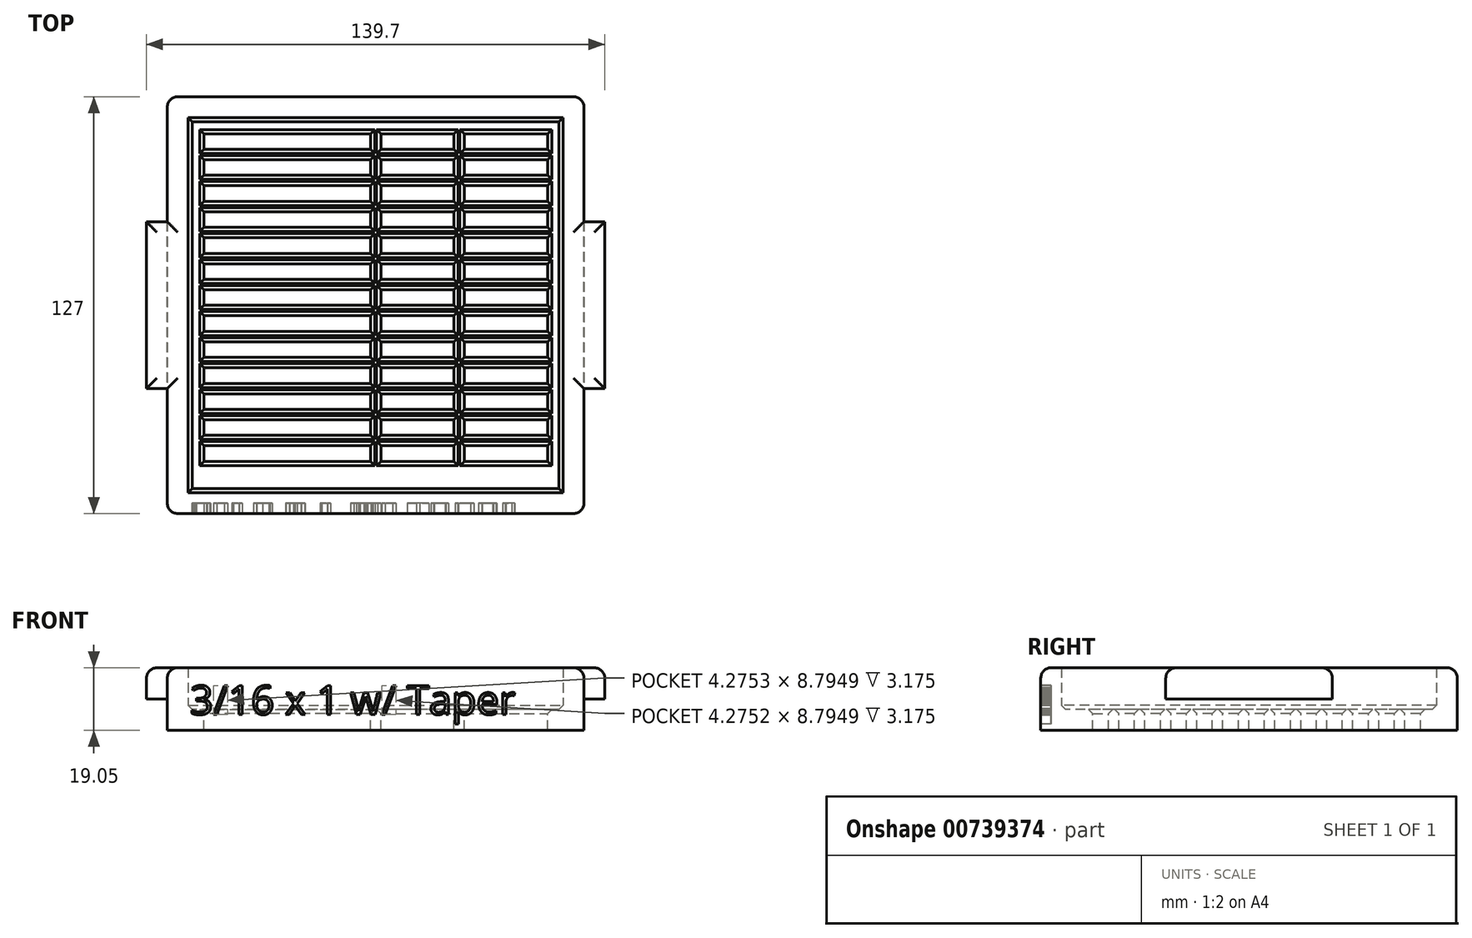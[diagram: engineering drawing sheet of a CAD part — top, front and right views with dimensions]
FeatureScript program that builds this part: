
annotation { "Feature Type Name" : "Feature", "Feature Type Description" : "" }
export const myFeature = defineFeature(function(context is Context, id is Id, definition is map)
    precondition{}
    {
        {
            var Q0;
            Q0=qCreatedBy(makeId("Top.planeOp"),FACE);
            var sketch = newSketch(context, id + "F0", { "sketchPlane" : qUnion([Q0])});
            skLineSegment(sketch, "E0.bottom", {"start": v(-63.5, -63.76) * mm, "end": v(63.5, -63.76) * mm});
            skLineSegment(sketch, "E0.top", {"start": v(-63.5, 63.24) * mm, "end": v(63.5, 63.24) * mm});
            skLineSegment(sketch, "E0.left", {"start": v(-63.5, -63.76) * mm, "end": v(-63.5, 63.24) * mm});
            skLineSegment(sketch, "E0.right", {"start": v(63.5, -63.76) * mm, "end": v(63.5, 63.24) * mm});
            skLineSegment(sketch, "E1.bottom", {"start": v(-57.15, -57.4) * mm, "end": v(57.15, -57.4) * mm});
            skLineSegment(sketch, "E1.top", {"start": v(-57.15, 56.9) * mm, "end": v(57.15, 56.9) * mm});
            skLineSegment(sketch, "E1.left", {"start": v(-57.15, -57.4) * mm, "end": v(-57.15, 56.9) * mm});
            skLineSegment(sketch, "E1.right", {"start": v(57.15, -57.4) * mm, "end": v(57.15, 56.9) * mm});
            skPoint(sketch, "E2", {"position": v(-63.5, -0.26) * mm});
            skPoint(sketch, "E3", {"position": v(63.5, -0.26) * mm});
            skLineSegment(sketch, "E4.bottom", {"start": v(-69.85, 25.14) * mm, "end": v(-57.15, 25.14) * mm});
            skLineSegment(sketch, "E4.top", {"start": v(-69.85, -25.66) * mm, "end": v(-57.15, -25.66) * mm});
            skLineSegment(sketch, "E4.left", {"start": v(-69.85, 25.14) * mm, "end": v(-69.85, -25.66) * mm});
            skLineSegment(sketch, "E4.right", {"start": v(-57.15, 25.14) * mm, "end": v(-57.15, -25.66) * mm});
            skLineSegment(sketch, "E5.bottom", {"start": v(69.85, 25.14) * mm, "end": v(57.15, 25.14) * mm});
            skLineSegment(sketch, "E5.top", {"start": v(69.85, -25.66) * mm, "end": v(57.15, -25.66) * mm});
            skLineSegment(sketch, "E5.left", {"start": v(69.85, 25.14) * mm, "end": v(69.85, -25.66) * mm});
            skLineSegment(sketch, "E5.right", {"start": v(57.15, 25.14) * mm, "end": v(57.15, -25.66) * mm});
            skPoint(sketch, "E5.cornerSnap0", {"position": v(-63.5, 25.14) * mm});
            skSolve(sketch);
        }
        {
            var Q0;
            {var subQ3=sQuery(id+"F0.wireOp",EDGE,"E1.bottom");Q0=makeQuery(id+"F0.imprint","IMPRINT",FACE,{"disambiguationData":[TD([[makeQuery(id+"F0.imprint","IMPRINT",EDGE,{"derivedFrom":subQ3}),1.0]])]});}
            extrude(context, id + "F1", {"entities" : qUnion([Q0]), "depth" : 6.35 * mm, "offsetDistance" : 25.4 * mm});
        }
        {
            var Q0;
            Q0=qSketchRegion(id+"F0",true);
            extrude(context, id + "F2", {"entities" : qUnion([Q0]), "operationType" : NewBodyOperationType.ADD, "depth" : 19.05 * mm, "offsetDistance" : 25.4 * mm});
        }
        {
            var Q0;
            Q0=makeQuery(id+"F1.opExtrude","CAP_FACE",FACE,{"disambiguationData":[OSD([sQuery(id+"F0.wireOp",EDGE,"E1.bottom"),sQuery(id+"F0.wireOp",EDGE,"E1.top"),sQuery(id+"F0.wireOp",EDGE,"E1.left"),sQuery(id+"F0.wireOp",EDGE,"E1.right"),sQuery(id+"F0.wireOp",EDGE,"E4.right"),sQuery(id+"F0.wireOp",EDGE,"E5.right")])],"isStart":false});
            var sketch = newSketch(context, id + "F3", { "sketchPlane" : qUnion([Q0])});
            skLineSegment(sketch, "E6.bottom", {"start": v(-52.4, -47.88) * mm, "end": v(-23.83, -47.88) * mm});
            skLineSegment(sketch, "E6.top", {"start": v(-52.4, -43.13) * mm, "end": v(-23.83, -43.13) * mm});
            skLineSegment(sketch, "E6.left", {"start": v(-52.4, -47.88) * mm, "end": v(-52.4, -43.13) * mm});
            skLineSegment(sketch, "E6.right", {"start": v(-23.83, -47.88) * mm, "end": v(-23.83, -43.13) * mm});
            skLineSegment(sketch, "E7.0.1.0", {"start": v(-52.4, -39.96) * mm, "end": v(-23.83, -39.96) * mm});
            skLineSegment(sketch, "E7.0.1.1", {"start": v(-52.4, -35.2) * mm, "end": v(-23.83, -35.2) * mm});
            skLineSegment(sketch, "E7.0.1.2", {"start": v(-52.4, -39.96) * mm, "end": v(-52.4, -35.2) * mm});
            skLineSegment(sketch, "E7.0.1.3", {"start": v(-23.83, -39.96) * mm, "end": v(-23.83, -35.2) * mm});
            skLineSegment(sketch, "E7.0.2.0", {"start": v(-52.4, -32.03) * mm, "end": v(-23.83, -32.03) * mm});
            skLineSegment(sketch, "E7.0.2.1", {"start": v(-52.4, -27.28) * mm, "end": v(-23.83, -27.28) * mm});
            skLineSegment(sketch, "E7.0.2.2", {"start": v(-52.4, -32.03) * mm, "end": v(-52.4, -27.28) * mm});
            skLineSegment(sketch, "E7.0.2.3", {"start": v(-23.83, -32.03) * mm, "end": v(-23.83, -27.28) * mm});
            skLineSegment(sketch, "E7.0.3.0", {"start": v(-52.4, -24.1) * mm, "end": v(-23.83, -24.1) * mm});
            skLineSegment(sketch, "E7.0.3.1", {"start": v(-52.4, -19.36) * mm, "end": v(-23.83, -19.36) * mm});
            skLineSegment(sketch, "E7.0.3.2", {"start": v(-52.4, -24.1) * mm, "end": v(-52.4, -19.36) * mm});
            skLineSegment(sketch, "E7.0.3.3", {"start": v(-23.83, -24.1) * mm, "end": v(-23.83, -19.36) * mm});
            skLineSegment(sketch, "E7.0.4.0", {"start": v(-52.4, -16.18) * mm, "end": v(-23.83, -16.18) * mm});
            skLineSegment(sketch, "E7.0.4.1", {"start": v(-52.4, -11.43) * mm, "end": v(-23.83, -11.43) * mm});
            skLineSegment(sketch, "E7.0.4.2", {"start": v(-52.4, -16.18) * mm, "end": v(-52.4, -11.43) * mm});
            skLineSegment(sketch, "E7.0.4.3", {"start": v(-23.83, -16.18) * mm, "end": v(-23.83, -11.43) * mm});
            skLineSegment(sketch, "E7.0.5.0", {"start": v(-52.4, -8.26) * mm, "end": v(-23.83, -8.26) * mm});
            skLineSegment(sketch, "E7.0.5.1", {"start": v(-52.4, -3.5) * mm, "end": v(-23.83, -3.5) * mm});
            skLineSegment(sketch, "E7.0.5.2", {"start": v(-52.4, -8.26) * mm, "end": v(-52.4, -3.5) * mm});
            skLineSegment(sketch, "E7.0.5.3", {"start": v(-23.83, -8.26) * mm, "end": v(-23.83, -3.5) * mm});
            skLineSegment(sketch, "E7.0.6.0", {"start": v(-52.4, -0.33) * mm, "end": v(-23.83, -0.33) * mm});
            skLineSegment(sketch, "E7.0.6.1", {"start": v(-52.4, 4.42) * mm, "end": v(-23.83, 4.42) * mm});
            skLineSegment(sketch, "E7.0.6.2", {"start": v(-52.4, -0.33) * mm, "end": v(-52.4, 4.42) * mm});
            skLineSegment(sketch, "E7.0.6.3", {"start": v(-23.83, -0.33) * mm, "end": v(-23.83, 4.42) * mm});
            skLineSegment(sketch, "E7.0.7.0", {"start": v(-52.4, 7.6) * mm, "end": v(-23.83, 7.6) * mm});
            skLineSegment(sketch, "E7.0.7.1", {"start": v(-52.4, 12.34) * mm, "end": v(-23.83, 12.34) * mm});
            skLineSegment(sketch, "E7.0.7.2", {"start": v(-52.4, 7.6) * mm, "end": v(-52.4, 12.34) * mm});
            skLineSegment(sketch, "E7.0.7.3", {"start": v(-23.83, 7.6) * mm, "end": v(-23.83, 12.34) * mm});
            skLineSegment(sketch, "E7.0.8.0", {"start": v(-52.4, 15.51) * mm, "end": v(-23.83, 15.51) * mm});
            skLineSegment(sketch, "E7.0.8.1", {"start": v(-52.4, 20.26) * mm, "end": v(-23.83, 20.26) * mm});
            skLineSegment(sketch, "E7.0.8.2", {"start": v(-52.4, 15.51) * mm, "end": v(-52.4, 20.26) * mm});
            skLineSegment(sketch, "E7.0.8.3", {"start": v(-23.83, 15.51) * mm, "end": v(-23.83, 20.26) * mm});
            skLineSegment(sketch, "E7.0.9.0", {"start": v(-52.4, 23.44) * mm, "end": v(-23.83, 23.44) * mm});
            skLineSegment(sketch, "E7.0.9.1", {"start": v(-52.4, 28.19) * mm, "end": v(-23.83, 28.19) * mm});
            skLineSegment(sketch, "E7.0.9.2", {"start": v(-52.4, 23.44) * mm, "end": v(-52.4, 28.19) * mm});
            skLineSegment(sketch, "E7.0.9.3", {"start": v(-23.83, 23.44) * mm, "end": v(-23.83, 28.19) * mm});
            skLineSegment(sketch, "E7.0.10.0", {"start": v(-52.4, 31.36) * mm, "end": v(-23.83, 31.36) * mm});
            skLineSegment(sketch, "E7.0.10.1", {"start": v(-52.4, 36.11) * mm, "end": v(-23.83, 36.11) * mm});
            skLineSegment(sketch, "E7.0.10.2", {"start": v(-52.4, 31.36) * mm, "end": v(-52.4, 36.11) * mm});
            skLineSegment(sketch, "E7.0.10.3", {"start": v(-23.83, 31.36) * mm, "end": v(-23.83, 36.11) * mm});
            skLineSegment(sketch, "E7.0.11.0", {"start": v(-52.4, 39.29) * mm, "end": v(-23.83, 39.29) * mm});
            skLineSegment(sketch, "E7.0.11.1", {"start": v(-52.4, 44.04) * mm, "end": v(-23.83, 44.04) * mm});
            skLineSegment(sketch, "E7.0.11.2", {"start": v(-52.4, 39.29) * mm, "end": v(-52.4, 44.04) * mm});
            skLineSegment(sketch, "E7.0.11.3", {"start": v(-23.83, 39.29) * mm, "end": v(-23.83, 44.04) * mm});
            skLineSegment(sketch, "E7.0.12.0", {"start": v(-52.4, 47.21) * mm, "end": v(-23.83, 47.21) * mm});
            skLineSegment(sketch, "E7.0.12.1", {"start": v(-52.4, 51.96) * mm, "end": v(-23.83, 51.96) * mm});
            skLineSegment(sketch, "E7.0.12.2", {"start": v(-52.4, 47.21) * mm, "end": v(-52.4, 51.96) * mm});
            skLineSegment(sketch, "E7.0.12.3", {"start": v(-23.83, 47.21) * mm, "end": v(-23.83, 51.96) * mm});
            skLineSegment(sketch, "E7.1.0.0", {"start": v(-27, -47.88) * mm, "end": v(1.57, -47.88) * mm});
            skLineSegment(sketch, "E7.1.0.1", {"start": v(-27, -43.13) * mm, "end": v(1.57, -43.13) * mm});
            skLineSegment(sketch, "E7.1.0.2", {"start": v(-27, -47.88) * mm, "end": v(-27, -43.13) * mm});
            skLineSegment(sketch, "E7.1.0.3", {"start": v(1.57, -47.88) * mm, "end": v(1.57, -43.13) * mm});
            skLineSegment(sketch, "E7.1.1.0", {"start": v(-27, -39.96) * mm, "end": v(1.57, -39.96) * mm});
            skLineSegment(sketch, "E7.1.1.1", {"start": v(-27, -35.2) * mm, "end": v(1.57, -35.2) * mm});
            skLineSegment(sketch, "E7.1.1.2", {"start": v(-27, -39.96) * mm, "end": v(-27, -35.2) * mm});
            skLineSegment(sketch, "E7.1.1.3", {"start": v(1.57, -39.96) * mm, "end": v(1.57, -35.2) * mm});
            skLineSegment(sketch, "E7.1.2.0", {"start": v(-27, -32.03) * mm, "end": v(1.57, -32.03) * mm});
            skLineSegment(sketch, "E7.1.2.1", {"start": v(-27, -27.28) * mm, "end": v(1.57, -27.28) * mm});
            skLineSegment(sketch, "E7.1.2.2", {"start": v(-27, -32.03) * mm, "end": v(-27, -27.28) * mm});
            skLineSegment(sketch, "E7.1.2.3", {"start": v(1.57, -32.03) * mm, "end": v(1.57, -27.28) * mm});
            skLineSegment(sketch, "E7.1.3.0", {"start": v(-27, -24.1) * mm, "end": v(1.57, -24.1) * mm});
            skLineSegment(sketch, "E7.1.3.1", {"start": v(-27, -19.36) * mm, "end": v(1.57, -19.36) * mm});
            skLineSegment(sketch, "E7.1.3.2", {"start": v(-27, -24.1) * mm, "end": v(-27, -19.36) * mm});
            skLineSegment(sketch, "E7.1.3.3", {"start": v(1.57, -24.1) * mm, "end": v(1.57, -19.36) * mm});
            skLineSegment(sketch, "E7.1.4.0", {"start": v(-27, -16.18) * mm, "end": v(1.57, -16.18) * mm});
            skLineSegment(sketch, "E7.1.4.1", {"start": v(-27, -11.43) * mm, "end": v(1.57, -11.43) * mm});
            skLineSegment(sketch, "E7.1.4.2", {"start": v(-27, -16.18) * mm, "end": v(-27, -11.43) * mm});
            skLineSegment(sketch, "E7.1.4.3", {"start": v(1.57, -16.18) * mm, "end": v(1.57, -11.43) * mm});
            skLineSegment(sketch, "E7.1.5.0", {"start": v(-27, -8.26) * mm, "end": v(1.57, -8.26) * mm});
            skLineSegment(sketch, "E7.1.5.1", {"start": v(-27, -3.5) * mm, "end": v(1.57, -3.5) * mm});
            skLineSegment(sketch, "E7.1.5.2", {"start": v(-27, -8.26) * mm, "end": v(-27, -3.5) * mm});
            skLineSegment(sketch, "E7.1.5.3", {"start": v(1.57, -8.26) * mm, "end": v(1.57, -3.5) * mm});
            skLineSegment(sketch, "E7.1.6.0", {"start": v(-27, -0.33) * mm, "end": v(1.57, -0.33) * mm});
            skLineSegment(sketch, "E7.1.6.1", {"start": v(-27, 4.42) * mm, "end": v(1.57, 4.42) * mm});
            skLineSegment(sketch, "E7.1.6.2", {"start": v(-27, -0.33) * mm, "end": v(-27, 4.42) * mm});
            skLineSegment(sketch, "E7.1.6.3", {"start": v(1.57, -0.33) * mm, "end": v(1.57, 4.42) * mm});
            skLineSegment(sketch, "E7.1.7.0", {"start": v(-27, 7.6) * mm, "end": v(1.57, 7.6) * mm});
            skLineSegment(sketch, "E7.1.7.1", {"start": v(-27, 12.34) * mm, "end": v(1.57, 12.34) * mm});
            skLineSegment(sketch, "E7.1.7.2", {"start": v(-27, 7.6) * mm, "end": v(-27, 12.34) * mm});
            skLineSegment(sketch, "E7.1.7.3", {"start": v(1.57, 7.6) * mm, "end": v(1.57, 12.34) * mm});
            skLineSegment(sketch, "E7.1.8.0", {"start": v(-27, 15.51) * mm, "end": v(1.57, 15.51) * mm});
            skLineSegment(sketch, "E7.1.8.1", {"start": v(-27, 20.26) * mm, "end": v(1.57, 20.26) * mm});
            skLineSegment(sketch, "E7.1.8.2", {"start": v(-27, 15.51) * mm, "end": v(-27, 20.26) * mm});
            skLineSegment(sketch, "E7.1.8.3", {"start": v(1.57, 15.51) * mm, "end": v(1.57, 20.26) * mm});
            skLineSegment(sketch, "E7.1.9.0", {"start": v(-27, 23.44) * mm, "end": v(1.57, 23.44) * mm});
            skLineSegment(sketch, "E7.1.9.1", {"start": v(-27, 28.19) * mm, "end": v(1.57, 28.19) * mm});
            skLineSegment(sketch, "E7.1.9.2", {"start": v(-27, 23.44) * mm, "end": v(-27, 28.19) * mm});
            skLineSegment(sketch, "E7.1.9.3", {"start": v(1.57, 23.44) * mm, "end": v(1.57, 28.19) * mm});
            skLineSegment(sketch, "E7.1.10.0", {"start": v(-27, 31.36) * mm, "end": v(1.57, 31.36) * mm});
            skLineSegment(sketch, "E7.1.10.1", {"start": v(-27, 36.11) * mm, "end": v(1.57, 36.11) * mm});
            skLineSegment(sketch, "E7.1.10.2", {"start": v(-27, 31.36) * mm, "end": v(-27, 36.11) * mm});
            skLineSegment(sketch, "E7.1.10.3", {"start": v(1.57, 31.36) * mm, "end": v(1.57, 36.11) * mm});
            skLineSegment(sketch, "E7.1.11.0", {"start": v(-27, 39.29) * mm, "end": v(1.57, 39.29) * mm});
            skLineSegment(sketch, "E7.1.11.1", {"start": v(-27, 44.04) * mm, "end": v(1.57, 44.04) * mm});
            skLineSegment(sketch, "E7.1.11.2", {"start": v(-27, 39.29) * mm, "end": v(-27, 44.04) * mm});
            skLineSegment(sketch, "E7.1.11.3", {"start": v(1.57, 39.29) * mm, "end": v(1.57, 44.04) * mm});
            skLineSegment(sketch, "E7.1.12.0", {"start": v(-27, 47.21) * mm, "end": v(1.57, 47.21) * mm});
            skLineSegment(sketch, "E7.1.12.1", {"start": v(-27, 51.96) * mm, "end": v(1.57, 51.96) * mm});
            skLineSegment(sketch, "E7.1.12.2", {"start": v(-27, 47.21) * mm, "end": v(-27, 51.96) * mm});
            skLineSegment(sketch, "E7.1.12.3", {"start": v(1.57, 47.21) * mm, "end": v(1.57, 51.96) * mm});
            skLineSegment(sketch, "E7.2.0.0", {"start": v(-1.6, -47.88) * mm, "end": v(26.97, -47.88) * mm});
            skLineSegment(sketch, "E7.2.0.1", {"start": v(-1.6, -43.13) * mm, "end": v(26.97, -43.13) * mm});
            skLineSegment(sketch, "E7.2.0.2", {"start": v(-1.6, -47.88) * mm, "end": v(-1.6, -43.13) * mm});
            skLineSegment(sketch, "E7.2.0.3", {"start": v(26.97, -47.88) * mm, "end": v(26.97, -43.13) * mm});
            skLineSegment(sketch, "E7.2.1.0", {"start": v(-1.6, -39.96) * mm, "end": v(26.97, -39.96) * mm});
            skLineSegment(sketch, "E7.2.1.1", {"start": v(-1.6, -35.2) * mm, "end": v(26.97, -35.2) * mm});
            skLineSegment(sketch, "E7.2.1.2", {"start": v(-1.6, -39.96) * mm, "end": v(-1.6, -35.2) * mm});
            skLineSegment(sketch, "E7.2.1.3", {"start": v(26.97, -39.96) * mm, "end": v(26.97, -35.2) * mm});
            skLineSegment(sketch, "E7.2.2.0", {"start": v(-1.6, -32.03) * mm, "end": v(26.97, -32.03) * mm});
            skLineSegment(sketch, "E7.2.2.1", {"start": v(-1.6, -27.28) * mm, "end": v(26.97, -27.28) * mm});
            skLineSegment(sketch, "E7.2.2.2", {"start": v(-1.6, -32.03) * mm, "end": v(-1.6, -27.28) * mm});
            skLineSegment(sketch, "E7.2.2.3", {"start": v(26.97, -32.03) * mm, "end": v(26.97, -27.28) * mm});
            skLineSegment(sketch, "E7.2.3.0", {"start": v(-1.6, -24.1) * mm, "end": v(26.97, -24.1) * mm});
            skLineSegment(sketch, "E7.2.3.1", {"start": v(-1.6, -19.36) * mm, "end": v(26.97, -19.36) * mm});
            skLineSegment(sketch, "E7.2.3.2", {"start": v(-1.6, -24.1) * mm, "end": v(-1.6, -19.36) * mm});
            skLineSegment(sketch, "E7.2.3.3", {"start": v(26.97, -24.1) * mm, "end": v(26.97, -19.36) * mm});
            skLineSegment(sketch, "E7.2.4.0", {"start": v(-1.6, -16.18) * mm, "end": v(26.97, -16.18) * mm});
            skLineSegment(sketch, "E7.2.4.1", {"start": v(-1.6, -11.43) * mm, "end": v(26.97, -11.43) * mm});
            skLineSegment(sketch, "E7.2.4.2", {"start": v(-1.6, -16.18) * mm, "end": v(-1.6, -11.43) * mm});
            skLineSegment(sketch, "E7.2.4.3", {"start": v(26.97, -16.18) * mm, "end": v(26.97, -11.43) * mm});
            skLineSegment(sketch, "E7.2.5.0", {"start": v(-1.6, -8.26) * mm, "end": v(26.97, -8.26) * mm});
            skLineSegment(sketch, "E7.2.5.1", {"start": v(-1.6, -3.5) * mm, "end": v(26.97, -3.5) * mm});
            skLineSegment(sketch, "E7.2.5.2", {"start": v(-1.6, -8.26) * mm, "end": v(-1.6, -3.5) * mm});
            skLineSegment(sketch, "E7.2.5.3", {"start": v(26.97, -8.26) * mm, "end": v(26.97, -3.5) * mm});
            skLineSegment(sketch, "E7.2.6.0", {"start": v(-1.6, -0.33) * mm, "end": v(26.97, -0.33) * mm});
            skLineSegment(sketch, "E7.2.6.1", {"start": v(-1.6, 4.42) * mm, "end": v(26.97, 4.42) * mm});
            skLineSegment(sketch, "E7.2.6.2", {"start": v(-1.6, -0.33) * mm, "end": v(-1.6, 4.42) * mm});
            skLineSegment(sketch, "E7.2.6.3", {"start": v(26.97, -0.33) * mm, "end": v(26.97, 4.42) * mm});
            skLineSegment(sketch, "E7.2.7.0", {"start": v(-1.6, 7.6) * mm, "end": v(26.97, 7.6) * mm});
            skLineSegment(sketch, "E7.2.7.1", {"start": v(-1.6, 12.34) * mm, "end": v(26.97, 12.34) * mm});
            skLineSegment(sketch, "E7.2.7.2", {"start": v(-1.6, 7.6) * mm, "end": v(-1.6, 12.34) * mm});
            skLineSegment(sketch, "E7.2.7.3", {"start": v(26.97, 7.6) * mm, "end": v(26.97, 12.34) * mm});
            skLineSegment(sketch, "E7.2.8.0", {"start": v(-1.6, 15.51) * mm, "end": v(26.97, 15.51) * mm});
            skLineSegment(sketch, "E7.2.8.1", {"start": v(-1.6, 20.26) * mm, "end": v(26.97, 20.26) * mm});
            skLineSegment(sketch, "E7.2.8.2", {"start": v(-1.6, 15.51) * mm, "end": v(-1.6, 20.26) * mm});
            skLineSegment(sketch, "E7.2.8.3", {"start": v(26.97, 15.51) * mm, "end": v(26.97, 20.26) * mm});
            skLineSegment(sketch, "E7.2.9.0", {"start": v(-1.6, 23.44) * mm, "end": v(26.97, 23.44) * mm});
            skLineSegment(sketch, "E7.2.9.1", {"start": v(-1.6, 28.19) * mm, "end": v(26.97, 28.19) * mm});
            skLineSegment(sketch, "E7.2.9.2", {"start": v(-1.6, 23.44) * mm, "end": v(-1.6, 28.19) * mm});
            skLineSegment(sketch, "E7.2.9.3", {"start": v(26.97, 23.44) * mm, "end": v(26.97, 28.19) * mm});
            skLineSegment(sketch, "E7.2.10.0", {"start": v(-1.6, 31.36) * mm, "end": v(26.97, 31.36) * mm});
            skLineSegment(sketch, "E7.2.10.1", {"start": v(-1.6, 36.11) * mm, "end": v(26.97, 36.11) * mm});
            skLineSegment(sketch, "E7.2.10.2", {"start": v(-1.6, 31.36) * mm, "end": v(-1.6, 36.11) * mm});
            skLineSegment(sketch, "E7.2.10.3", {"start": v(26.97, 31.36) * mm, "end": v(26.97, 36.11) * mm});
            skLineSegment(sketch, "E7.2.11.0", {"start": v(-1.6, 39.29) * mm, "end": v(26.97, 39.29) * mm});
            skLineSegment(sketch, "E7.2.11.1", {"start": v(-1.6, 44.04) * mm, "end": v(26.97, 44.04) * mm});
            skLineSegment(sketch, "E7.2.11.2", {"start": v(-1.6, 39.29) * mm, "end": v(-1.6, 44.04) * mm});
            skLineSegment(sketch, "E7.2.11.3", {"start": v(26.97, 39.29) * mm, "end": v(26.97, 44.04) * mm});
            skLineSegment(sketch, "E7.2.12.0", {"start": v(-1.6, 47.21) * mm, "end": v(26.97, 47.21) * mm});
            skLineSegment(sketch, "E7.2.12.1", {"start": v(-1.6, 51.96) * mm, "end": v(26.97, 51.96) * mm});
            skLineSegment(sketch, "E7.2.12.2", {"start": v(-1.6, 47.21) * mm, "end": v(-1.6, 51.96) * mm});
            skLineSegment(sketch, "E7.2.12.3", {"start": v(26.97, 47.21) * mm, "end": v(26.97, 51.96) * mm});
            skLineSegment(sketch, "E7.3.0.0", {"start": v(23.8, -47.88) * mm, "end": v(52.37, -47.88) * mm});
            skLineSegment(sketch, "E7.3.0.1", {"start": v(23.8, -43.13) * mm, "end": v(52.37, -43.13) * mm});
            skLineSegment(sketch, "E7.3.0.2", {"start": v(23.8, -47.88) * mm, "end": v(23.8, -43.13) * mm});
            skLineSegment(sketch, "E7.3.0.3", {"start": v(52.37, -47.88) * mm, "end": v(52.37, -43.13) * mm});
            skLineSegment(sketch, "E7.3.1.0", {"start": v(23.8, -39.96) * mm, "end": v(52.37, -39.96) * mm});
            skLineSegment(sketch, "E7.3.1.1", {"start": v(23.8, -35.2) * mm, "end": v(52.37, -35.2) * mm});
            skLineSegment(sketch, "E7.3.1.2", {"start": v(23.8, -39.96) * mm, "end": v(23.8, -35.2) * mm});
            skLineSegment(sketch, "E7.3.1.3", {"start": v(52.37, -39.96) * mm, "end": v(52.37, -35.2) * mm});
            skLineSegment(sketch, "E7.3.2.0", {"start": v(23.8, -32.03) * mm, "end": v(52.37, -32.03) * mm});
            skLineSegment(sketch, "E7.3.2.1", {"start": v(23.8, -27.28) * mm, "end": v(52.37, -27.28) * mm});
            skLineSegment(sketch, "E7.3.2.2", {"start": v(23.8, -32.03) * mm, "end": v(23.8, -27.28) * mm});
            skLineSegment(sketch, "E7.3.2.3", {"start": v(52.37, -32.03) * mm, "end": v(52.37, -27.28) * mm});
            skLineSegment(sketch, "E7.3.3.0", {"start": v(23.8, -24.1) * mm, "end": v(52.37, -24.1) * mm});
            skLineSegment(sketch, "E7.3.3.1", {"start": v(23.8, -19.36) * mm, "end": v(52.37, -19.36) * mm});
            skLineSegment(sketch, "E7.3.3.2", {"start": v(23.8, -24.1) * mm, "end": v(23.8, -19.36) * mm});
            skLineSegment(sketch, "E7.3.3.3", {"start": v(52.37, -24.1) * mm, "end": v(52.37, -19.36) * mm});
            skLineSegment(sketch, "E7.3.4.0", {"start": v(23.8, -16.18) * mm, "end": v(52.37, -16.18) * mm});
            skLineSegment(sketch, "E7.3.4.1", {"start": v(23.8, -11.43) * mm, "end": v(52.37, -11.43) * mm});
            skLineSegment(sketch, "E7.3.4.2", {"start": v(23.8, -16.18) * mm, "end": v(23.8, -11.43) * mm});
            skLineSegment(sketch, "E7.3.4.3", {"start": v(52.37, -16.18) * mm, "end": v(52.37, -11.43) * mm});
            skLineSegment(sketch, "E7.3.5.0", {"start": v(23.8, -8.26) * mm, "end": v(52.37, -8.26) * mm});
            skLineSegment(sketch, "E7.3.5.1", {"start": v(23.8, -3.5) * mm, "end": v(52.37, -3.5) * mm});
            skLineSegment(sketch, "E7.3.5.2", {"start": v(23.8, -8.26) * mm, "end": v(23.8, -3.5) * mm});
            skLineSegment(sketch, "E7.3.5.3", {"start": v(52.37, -8.26) * mm, "end": v(52.37, -3.5) * mm});
            skLineSegment(sketch, "E7.3.6.0", {"start": v(23.8, -0.33) * mm, "end": v(52.37, -0.33) * mm});
            skLineSegment(sketch, "E7.3.6.1", {"start": v(23.8, 4.42) * mm, "end": v(52.37, 4.42) * mm});
            skLineSegment(sketch, "E7.3.6.2", {"start": v(23.8, -0.33) * mm, "end": v(23.8, 4.42) * mm});
            skLineSegment(sketch, "E7.3.6.3", {"start": v(52.37, -0.33) * mm, "end": v(52.37, 4.42) * mm});
            skLineSegment(sketch, "E7.3.7.0", {"start": v(23.8, 7.6) * mm, "end": v(52.37, 7.6) * mm});
            skLineSegment(sketch, "E7.3.7.1", {"start": v(23.8, 12.34) * mm, "end": v(52.37, 12.34) * mm});
            skLineSegment(sketch, "E7.3.7.2", {"start": v(23.8, 7.6) * mm, "end": v(23.8, 12.34) * mm});
            skLineSegment(sketch, "E7.3.7.3", {"start": v(52.37, 7.6) * mm, "end": v(52.37, 12.34) * mm});
            skLineSegment(sketch, "E7.3.8.0", {"start": v(23.8, 15.51) * mm, "end": v(52.37, 15.51) * mm});
            skLineSegment(sketch, "E7.3.8.1", {"start": v(23.8, 20.26) * mm, "end": v(52.37, 20.26) * mm});
            skLineSegment(sketch, "E7.3.8.2", {"start": v(23.8, 15.51) * mm, "end": v(23.8, 20.26) * mm});
            skLineSegment(sketch, "E7.3.8.3", {"start": v(52.37, 15.51) * mm, "end": v(52.37, 20.26) * mm});
            skLineSegment(sketch, "E7.3.9.0", {"start": v(23.8, 23.44) * mm, "end": v(52.37, 23.44) * mm});
            skLineSegment(sketch, "E7.3.9.1", {"start": v(23.8, 28.19) * mm, "end": v(52.37, 28.19) * mm});
            skLineSegment(sketch, "E7.3.9.2", {"start": v(23.8, 23.44) * mm, "end": v(23.8, 28.19) * mm});
            skLineSegment(sketch, "E7.3.9.3", {"start": v(52.37, 23.44) * mm, "end": v(52.37, 28.19) * mm});
            skLineSegment(sketch, "E7.3.10.0", {"start": v(23.8, 31.36) * mm, "end": v(52.37, 31.36) * mm});
            skLineSegment(sketch, "E7.3.10.1", {"start": v(23.8, 36.11) * mm, "end": v(52.37, 36.11) * mm});
            skLineSegment(sketch, "E7.3.10.2", {"start": v(23.8, 31.36) * mm, "end": v(23.8, 36.11) * mm});
            skLineSegment(sketch, "E7.3.10.3", {"start": v(52.37, 31.36) * mm, "end": v(52.37, 36.11) * mm});
            skLineSegment(sketch, "E7.3.11.0", {"start": v(23.8, 39.29) * mm, "end": v(52.37, 39.29) * mm});
            skLineSegment(sketch, "E7.3.11.1", {"start": v(23.8, 44.04) * mm, "end": v(52.37, 44.04) * mm});
            skLineSegment(sketch, "E7.3.11.2", {"start": v(23.8, 39.29) * mm, "end": v(23.8, 44.04) * mm});
            skLineSegment(sketch, "E7.3.11.3", {"start": v(52.37, 39.29) * mm, "end": v(52.37, 44.04) * mm});
            skLineSegment(sketch, "E7.3.12.0", {"start": v(23.8, 47.21) * mm, "end": v(52.37, 47.21) * mm});
            skLineSegment(sketch, "E7.3.12.1", {"start": v(23.8, 51.96) * mm, "end": v(52.37, 51.96) * mm});
            skLineSegment(sketch, "E7.3.12.2", {"start": v(23.8, 47.21) * mm, "end": v(23.8, 51.96) * mm});
            skLineSegment(sketch, "E7.3.12.3", {"start": v(52.37, 47.21) * mm, "end": v(52.37, 51.96) * mm});
            skLineSegment(sketch, "E7.direction1", {"start": v(-52.4, -47.88) * mm, "end": v(-27, -47.88) * mm, "construction": true});
            skLineSegment(sketch, "E7.direction2", {"start": v(-52.4, -47.88) * mm, "end": v(-52.4, -39.96) * mm, "construction": true});
            skSolve(sketch);
        }
        {
            var Q0;
            Q0=makeQuery(id+"F3.imprint","IMPRINT",FACE,{"disambiguationData":[TD([[makeQuery(id+"F3.imprint","IMPRINT",EDGE,{"derivedFrom":sQuery(id+"F3.wireOp",EDGE,"E6.bottom")}),1.0]])]});
            var Q1;
            Q1=makeQuery(id+"F3.imprint","IMPRINT",FACE,{"disambiguationData":[TD([[makeQuery(id+"F3.imprint","IMPRINT",EDGE,{"derivedFrom":sQuery(id+"F3.wireOp",EDGE,"E7.0.1.0")}),1.0]])]});
            var Q2;
            Q2=makeQuery(id+"F3.imprint","IMPRINT",FACE,{"disambiguationData":[TD([[makeQuery(id+"F3.imprint","IMPRINT",EDGE,{"derivedFrom":sQuery(id+"F3.wireOp",EDGE,"E7.0.2.0")}),1.0]])]});
            var Q3;
            Q3=makeQuery(id+"F3.imprint","IMPRINT",FACE,{"disambiguationData":[TD([[makeQuery(id+"F3.imprint","IMPRINT",EDGE,{"derivedFrom":sQuery(id+"F3.wireOp",EDGE,"E7.0.3.0")}),1.0]])]});
            var Q4;
            Q4=makeQuery(id+"F3.imprint","IMPRINT",FACE,{"disambiguationData":[TD([[makeQuery(id+"F3.imprint","IMPRINT",EDGE,{"derivedFrom":sQuery(id+"F3.wireOp",EDGE,"E7.0.4.0")}),1.0]])]});
            var Q5;
            Q5=makeQuery(id+"F3.imprint","IMPRINT",FACE,{"disambiguationData":[TD([[makeQuery(id+"F3.imprint","IMPRINT",EDGE,{"derivedFrom":sQuery(id+"F3.wireOp",EDGE,"E7.0.5.0")}),1.0]])]});
            var Q6;
            Q6=makeQuery(id+"F3.imprint","IMPRINT",FACE,{"disambiguationData":[TD([[makeQuery(id+"F3.imprint","IMPRINT",EDGE,{"derivedFrom":sQuery(id+"F3.wireOp",EDGE,"E7.0.6.0")}),1.0]])]});
            var Q7;
            Q7=makeQuery(id+"F3.imprint","IMPRINT",FACE,{"disambiguationData":[TD([[makeQuery(id+"F3.imprint","IMPRINT",EDGE,{"derivedFrom":sQuery(id+"F3.wireOp",EDGE,"E7.0.7.0")}),1.0]])]});
            var Q8;
            Q8=makeQuery(id+"F3.imprint","IMPRINT",FACE,{"disambiguationData":[TD([[makeQuery(id+"F3.imprint","IMPRINT",EDGE,{"derivedFrom":sQuery(id+"F3.wireOp",EDGE,"E7.0.8.0")}),1.0]])]});
            var Q9;
            Q9=makeQuery(id+"F3.imprint","IMPRINT",FACE,{"disambiguationData":[TD([[makeQuery(id+"F3.imprint","IMPRINT",EDGE,{"derivedFrom":sQuery(id+"F3.wireOp",EDGE,"E7.0.9.0")}),1.0]])]});
            var Q10;
            Q10=makeQuery(id+"F3.imprint","IMPRINT",FACE,{"disambiguationData":[TD([[makeQuery(id+"F3.imprint","IMPRINT",EDGE,{"derivedFrom":sQuery(id+"F3.wireOp",EDGE,"E7.0.10.0")}),1.0]])]});
            var Q11;
            Q11=makeQuery(id+"F3.imprint","IMPRINT",FACE,{"disambiguationData":[TD([[makeQuery(id+"F3.imprint","IMPRINT",EDGE,{"derivedFrom":sQuery(id+"F3.wireOp",EDGE,"E7.0.11.0")}),1.0]])]});
            var Q12;
            Q12=makeQuery(id+"F3.imprint","IMPRINT",FACE,{"disambiguationData":[TD([[makeQuery(id+"F3.imprint","IMPRINT",EDGE,{"derivedFrom":sQuery(id+"F3.wireOp",EDGE,"E7.0.12.0")}),1.0]])]});
            var Q13;
            Q13=makeQuery(id+"F3.imprint","IMPRINT",FACE,{"disambiguationData":[TD([[makeQuery(id+"F3.imprint","IMPRINT",EDGE,{"derivedFrom":sQuery(id+"F3.wireOp",EDGE,"E7.0.13.0")}),1.0]])]});
            var Q14;
            Q14=makeQuery(id+"F3.imprint","IMPRINT",FACE,{"disambiguationData":[TD([[makeQuery(id+"F3.imprint","IMPRINT",EDGE,{"derivedFrom":sQuery(id+"F3.wireOp",EDGE,"E7.0.14.0")}),1.0]])]});
            var Q15;
            Q15=makeQuery(id+"F3.imprint","IMPRINT",FACE,{"disambiguationData":[TD([[makeQuery(id+"F3.imprint","IMPRINT",EDGE,{"derivedFrom":sQuery(id+"F3.wireOp",EDGE,"E7.0.15.0")}),1.0]])]});
            var Q16;
            Q16=makeQuery(id+"F3.imprint","IMPRINT",FACE,{"disambiguationData":[TD([[makeQuery(id+"F3.imprint","IMPRINT",EDGE,{"derivedFrom":sQuery(id+"F3.wireOp",EDGE,"E7.0.16.0")}),1.0]])]});
            var Q17;
            Q17=makeQuery(id+"F3.imprint","IMPRINT",FACE,{"disambiguationData":[TD([[makeQuery(id+"F3.imprint","IMPRINT",EDGE,{"derivedFrom":sQuery(id+"F3.wireOp",EDGE,"E7.0.17.0")}),1.0]])]});
            var Q18;
            Q18=makeQuery(id+"F3.imprint","IMPRINT",FACE,{"disambiguationData":[TD([[makeQuery(id+"F3.imprint","IMPRINT",EDGE,{"derivedFrom":sQuery(id+"F3.wireOp",EDGE,"E7.0.18.0")}),1.0]])]});
            var Q19;
            Q19=makeQuery(id+"F3.imprint","IMPRINT",FACE,{"disambiguationData":[TD([[makeQuery(id+"F3.imprint","IMPRINT",EDGE,{"derivedFrom":sQuery(id+"F3.wireOp",EDGE,"E7.0.19.0")}),1.0]])]});
            var Q20;
            Q20=makeQuery(id+"F3.imprint","IMPRINT",FACE,{"disambiguationData":[TD([[makeQuery(id+"F3.imprint","IMPRINT",EDGE,{"derivedFrom":sQuery(id+"F3.wireOp",EDGE,"E7.0.20.0")}),1.0]])]});
            var Q21;
            Q21=makeQuery(id+"F3.imprint","IMPRINT",FACE,{"disambiguationData":[TD([[makeQuery(id+"F3.imprint","IMPRINT",EDGE,{"derivedFrom":sQuery(id+"F3.wireOp",EDGE,"E7.0.21.0")}),1.0]])]});
            var Q22;
            {var subQ0=sQuery(id+"F3.wireOp",EDGE,"E6.right");Q22=makeQuery(id+"F3.imprint","IMPRINT",FACE,{"disambiguationData":[TD([[makeQuery(id+"F3.imprint","IMPRINT",EDGE,{"derivedFrom":subQ0}),-1.0]])]});}
            var Q23;
            {var subQ0=sQuery(id+"F3.wireOp",EDGE,"E7.0.1.3");Q23=makeQuery(id+"F3.imprint","IMPRINT",FACE,{"disambiguationData":[TD([[makeQuery(id+"F3.imprint","IMPRINT",EDGE,{"derivedFrom":subQ0}),-1.0]])]});}
            var Q24;
            {var subQ0=sQuery(id+"F3.wireOp",EDGE,"E7.1.0.3");Q24=makeQuery(id+"F3.imprint","IMPRINT",FACE,{"disambiguationData":[TD([[makeQuery(id+"F3.imprint","IMPRINT",EDGE,{"derivedFrom":subQ0}),-1.0]])]});}
            var Q25;
            {var subQ0=sQuery(id+"F3.wireOp",EDGE,"E7.1.1.3");Q25=makeQuery(id+"F3.imprint","IMPRINT",FACE,{"disambiguationData":[TD([[makeQuery(id+"F3.imprint","IMPRINT",EDGE,{"derivedFrom":subQ0}),-1.0]])]});}
            var Q26;
            {var subQ0=sQuery(id+"F3.wireOp",EDGE,"E7.2.0.3");Q26=makeQuery(id+"F3.imprint","IMPRINT",FACE,{"disambiguationData":[TD([[makeQuery(id+"F3.imprint","IMPRINT",EDGE,{"derivedFrom":subQ0}),-1.0]])]});}
            var Q27;
            {var subQ0=sQuery(id+"F3.wireOp",EDGE,"E7.2.1.3");Q27=makeQuery(id+"F3.imprint","IMPRINT",FACE,{"disambiguationData":[TD([[makeQuery(id+"F3.imprint","IMPRINT",EDGE,{"derivedFrom":subQ0}),-1.0]])]});}
            var Q28;
            {var subQ0=sQuery(id+"F3.wireOp",EDGE,"E7.2.2.3");Q28=makeQuery(id+"F3.imprint","IMPRINT",FACE,{"disambiguationData":[TD([[makeQuery(id+"F3.imprint","IMPRINT",EDGE,{"derivedFrom":subQ0}),-1.0]])]});}
            var Q29;
            {var subQ0=sQuery(id+"F3.wireOp",EDGE,"E7.2.3.3");Q29=makeQuery(id+"F3.imprint","IMPRINT",FACE,{"disambiguationData":[TD([[makeQuery(id+"F3.imprint","IMPRINT",EDGE,{"derivedFrom":subQ0}),-1.0]])]});}
            var Q30;
            {var subQ0=sQuery(id+"F3.wireOp",EDGE,"E7.1.3.3");Q30=makeQuery(id+"F3.imprint","IMPRINT",FACE,{"disambiguationData":[TD([[makeQuery(id+"F3.imprint","IMPRINT",EDGE,{"derivedFrom":subQ0}),-1.0]])]});}
            var Q31;
            {var subQ0=sQuery(id+"F3.wireOp",EDGE,"E7.1.2.3");Q31=makeQuery(id+"F3.imprint","IMPRINT",FACE,{"disambiguationData":[TD([[makeQuery(id+"F3.imprint","IMPRINT",EDGE,{"derivedFrom":subQ0}),-1.0]])]});}
            var Q32;
            {var subQ0=sQuery(id+"F3.wireOp",EDGE,"E7.0.2.3");Q32=makeQuery(id+"F3.imprint","IMPRINT",FACE,{"disambiguationData":[TD([[makeQuery(id+"F3.imprint","IMPRINT",EDGE,{"derivedFrom":subQ0}),-1.0]])]});}
            var Q33;
            {var subQ0=sQuery(id+"F3.wireOp",EDGE,"E7.0.3.3");Q33=makeQuery(id+"F3.imprint","IMPRINT",FACE,{"disambiguationData":[TD([[makeQuery(id+"F3.imprint","IMPRINT",EDGE,{"derivedFrom":subQ0}),-1.0]])]});}
            var Q34;
            {var subQ0=sQuery(id+"F3.wireOp",EDGE,"E7.2.4.3");Q34=makeQuery(id+"F3.imprint","IMPRINT",FACE,{"disambiguationData":[TD([[makeQuery(id+"F3.imprint","IMPRINT",EDGE,{"derivedFrom":subQ0}),-1.0]])]});}
            var Q35;
            {var subQ0=sQuery(id+"F3.wireOp",EDGE,"E7.2.5.3");Q35=makeQuery(id+"F3.imprint","IMPRINT",FACE,{"disambiguationData":[TD([[makeQuery(id+"F3.imprint","IMPRINT",EDGE,{"derivedFrom":subQ0}),-1.0]])]});}
            var Q36;
            {var subQ0=sQuery(id+"F3.wireOp",EDGE,"E7.2.6.3");Q36=makeQuery(id+"F3.imprint","IMPRINT",FACE,{"disambiguationData":[TD([[makeQuery(id+"F3.imprint","IMPRINT",EDGE,{"derivedFrom":subQ0}),-1.0]])]});}
            var Q37;
            {var subQ0=sQuery(id+"F3.wireOp",EDGE,"E7.1.4.3");Q37=makeQuery(id+"F3.imprint","IMPRINT",FACE,{"disambiguationData":[TD([[makeQuery(id+"F3.imprint","IMPRINT",EDGE,{"derivedFrom":subQ0}),-1.0]])]});}
            var Q38;
            {var subQ0=sQuery(id+"F3.wireOp",EDGE,"E7.1.5.3");Q38=makeQuery(id+"F3.imprint","IMPRINT",FACE,{"disambiguationData":[TD([[makeQuery(id+"F3.imprint","IMPRINT",EDGE,{"derivedFrom":subQ0}),-1.0]])]});}
            var Q39;
            {var subQ0=sQuery(id+"F3.wireOp",EDGE,"E7.1.6.3");Q39=makeQuery(id+"F3.imprint","IMPRINT",FACE,{"disambiguationData":[TD([[makeQuery(id+"F3.imprint","IMPRINT",EDGE,{"derivedFrom":subQ0}),-1.0]])]});}
            var Q40;
            {var subQ0=sQuery(id+"F3.wireOp",EDGE,"E7.0.4.3");Q40=makeQuery(id+"F3.imprint","IMPRINT",FACE,{"disambiguationData":[TD([[makeQuery(id+"F3.imprint","IMPRINT",EDGE,{"derivedFrom":subQ0}),-1.0]])]});}
            var Q41;
            {var subQ0=sQuery(id+"F3.wireOp",EDGE,"E7.0.5.3");Q41=makeQuery(id+"F3.imprint","IMPRINT",FACE,{"disambiguationData":[TD([[makeQuery(id+"F3.imprint","IMPRINT",EDGE,{"derivedFrom":subQ0}),-1.0]])]});}
            var Q42;
            {var subQ0=sQuery(id+"F3.wireOp",EDGE,"E7.0.6.3");Q42=makeQuery(id+"F3.imprint","IMPRINT",FACE,{"disambiguationData":[TD([[makeQuery(id+"F3.imprint","IMPRINT",EDGE,{"derivedFrom":subQ0}),-1.0]])]});}
            var Q43;
            {var subQ0=sQuery(id+"F3.wireOp",EDGE,"E7.0.7.3");Q43=makeQuery(id+"F3.imprint","IMPRINT",FACE,{"disambiguationData":[TD([[makeQuery(id+"F3.imprint","IMPRINT",EDGE,{"derivedFrom":subQ0}),-1.0]])]});}
            var Q44;
            {var subQ0=sQuery(id+"F3.wireOp",EDGE,"E7.0.8.3");Q44=makeQuery(id+"F3.imprint","IMPRINT",FACE,{"disambiguationData":[TD([[makeQuery(id+"F3.imprint","IMPRINT",EDGE,{"derivedFrom":subQ0}),-1.0]])]});}
            var Q45;
            {var subQ0=sQuery(id+"F3.wireOp",EDGE,"E7.0.9.3");Q45=makeQuery(id+"F3.imprint","IMPRINT",FACE,{"disambiguationData":[TD([[makeQuery(id+"F3.imprint","IMPRINT",EDGE,{"derivedFrom":subQ0}),-1.0]])]});}
            var Q46;
            {var subQ0=sQuery(id+"F3.wireOp",EDGE,"E7.0.10.3");Q46=makeQuery(id+"F3.imprint","IMPRINT",FACE,{"disambiguationData":[TD([[makeQuery(id+"F3.imprint","IMPRINT",EDGE,{"derivedFrom":subQ0}),-1.0]])]});}
            var Q47;
            {var subQ0=sQuery(id+"F3.wireOp",EDGE,"E7.1.7.3");Q47=makeQuery(id+"F3.imprint","IMPRINT",FACE,{"disambiguationData":[TD([[makeQuery(id+"F3.imprint","IMPRINT",EDGE,{"derivedFrom":subQ0}),-1.0]])]});}
            var Q48;
            {var subQ0=sQuery(id+"F3.wireOp",EDGE,"E7.1.8.3");Q48=makeQuery(id+"F3.imprint","IMPRINT",FACE,{"disambiguationData":[TD([[makeQuery(id+"F3.imprint","IMPRINT",EDGE,{"derivedFrom":subQ0}),-1.0]])]});}
            var Q49;
            {var subQ0=sQuery(id+"F3.wireOp",EDGE,"E7.1.9.3");Q49=makeQuery(id+"F3.imprint","IMPRINT",FACE,{"disambiguationData":[TD([[makeQuery(id+"F3.imprint","IMPRINT",EDGE,{"derivedFrom":subQ0}),-1.0]])]});}
            var Q50;
            {var subQ0=sQuery(id+"F3.wireOp",EDGE,"E7.1.10.3");Q50=makeQuery(id+"F3.imprint","IMPRINT",FACE,{"disambiguationData":[TD([[makeQuery(id+"F3.imprint","IMPRINT",EDGE,{"derivedFrom":subQ0}),-1.0]])]});}
            var Q51;
            {var subQ0=sQuery(id+"F3.wireOp",EDGE,"E7.2.10.3");Q51=makeQuery(id+"F3.imprint","IMPRINT",FACE,{"disambiguationData":[TD([[makeQuery(id+"F3.imprint","IMPRINT",EDGE,{"derivedFrom":subQ0}),-1.0]])]});}
            var Q52;
            {var subQ0=sQuery(id+"F3.wireOp",EDGE,"E7.2.9.3");Q52=makeQuery(id+"F3.imprint","IMPRINT",FACE,{"disambiguationData":[TD([[makeQuery(id+"F3.imprint","IMPRINT",EDGE,{"derivedFrom":subQ0}),-1.0]])]});}
            var Q53;
            {var subQ0=sQuery(id+"F3.wireOp",EDGE,"E7.2.8.3");Q53=makeQuery(id+"F3.imprint","IMPRINT",FACE,{"disambiguationData":[TD([[makeQuery(id+"F3.imprint","IMPRINT",EDGE,{"derivedFrom":subQ0}),-1.0]])]});}
            var Q54;
            {var subQ0=sQuery(id+"F3.wireOp",EDGE,"E7.2.7.3");Q54=makeQuery(id+"F3.imprint","IMPRINT",FACE,{"disambiguationData":[TD([[makeQuery(id+"F3.imprint","IMPRINT",EDGE,{"derivedFrom":subQ0}),-1.0]])]});}
            var Q55;
            {var subQ0=sQuery(id+"F3.wireOp",EDGE,"E7.0.11.3");Q55=makeQuery(id+"F3.imprint","IMPRINT",FACE,{"disambiguationData":[TD([[makeQuery(id+"F3.imprint","IMPRINT",EDGE,{"derivedFrom":subQ0}),-1.0]])]});}
            var Q56;
            {var subQ0=sQuery(id+"F3.wireOp",EDGE,"E7.0.12.3");Q56=makeQuery(id+"F3.imprint","IMPRINT",FACE,{"disambiguationData":[TD([[makeQuery(id+"F3.imprint","IMPRINT",EDGE,{"derivedFrom":subQ0}),-1.0]])]});}
            var Q57;
            {var subQ0=sQuery(id+"F3.wireOp",EDGE,"E7.0.13.3");Q57=makeQuery(id+"F3.imprint","IMPRINT",FACE,{"disambiguationData":[TD([[makeQuery(id+"F3.imprint","IMPRINT",EDGE,{"derivedFrom":subQ0}),-1.0]])]});}
            var Q58;
            {var subQ0=sQuery(id+"F3.wireOp",EDGE,"E7.0.14.3");Q58=makeQuery(id+"F3.imprint","IMPRINT",FACE,{"disambiguationData":[TD([[makeQuery(id+"F3.imprint","IMPRINT",EDGE,{"derivedFrom":subQ0}),-1.0]])]});}
            var Q59;
            {var subQ0=sQuery(id+"F3.wireOp",EDGE,"E7.0.15.3");Q59=makeQuery(id+"F3.imprint","IMPRINT",FACE,{"disambiguationData":[TD([[makeQuery(id+"F3.imprint","IMPRINT",EDGE,{"derivedFrom":subQ0}),-1.0]])]});}
            var Q60;
            {var subQ0=sQuery(id+"F3.wireOp",EDGE,"E7.0.16.3");Q60=makeQuery(id+"F3.imprint","IMPRINT",FACE,{"disambiguationData":[TD([[makeQuery(id+"F3.imprint","IMPRINT",EDGE,{"derivedFrom":subQ0}),-1.0]])]});}
            var Q61;
            {var subQ0=sQuery(id+"F3.wireOp",EDGE,"E7.0.17.3");Q61=makeQuery(id+"F3.imprint","IMPRINT",FACE,{"disambiguationData":[TD([[makeQuery(id+"F3.imprint","IMPRINT",EDGE,{"derivedFrom":subQ0}),-1.0]])]});}
            var Q62;
            {var subQ0=sQuery(id+"F3.wireOp",EDGE,"E7.0.18.3");Q62=makeQuery(id+"F3.imprint","IMPRINT",FACE,{"disambiguationData":[TD([[makeQuery(id+"F3.imprint","IMPRINT",EDGE,{"derivedFrom":subQ0}),-1.0]])]});}
            var Q63;
            {var subQ0=sQuery(id+"F3.wireOp",EDGE,"E7.0.19.3");Q63=makeQuery(id+"F3.imprint","IMPRINT",FACE,{"disambiguationData":[TD([[makeQuery(id+"F3.imprint","IMPRINT",EDGE,{"derivedFrom":subQ0}),-1.0]])]});}
            var Q64;
            {var subQ0=sQuery(id+"F3.wireOp",EDGE,"E7.0.20.3");Q64=makeQuery(id+"F3.imprint","IMPRINT",FACE,{"disambiguationData":[TD([[makeQuery(id+"F3.imprint","IMPRINT",EDGE,{"derivedFrom":subQ0}),-1.0]])]});}
            var Q65;
            {var subQ0=sQuery(id+"F3.wireOp",EDGE,"E7.0.21.3");Q65=makeQuery(id+"F3.imprint","IMPRINT",FACE,{"disambiguationData":[TD([[makeQuery(id+"F3.imprint","IMPRINT",EDGE,{"derivedFrom":subQ0}),-1.0]])]});}
            var Q66;
            {var subQ0=sQuery(id+"F3.wireOp",EDGE,"E7.1.21.3");Q66=makeQuery(id+"F3.imprint","IMPRINT",FACE,{"disambiguationData":[TD([[makeQuery(id+"F3.imprint","IMPRINT",EDGE,{"derivedFrom":subQ0}),-1.0]])]});}
            var Q67;
            {var subQ0=sQuery(id+"F3.wireOp",EDGE,"E7.1.20.3");Q67=makeQuery(id+"F3.imprint","IMPRINT",FACE,{"disambiguationData":[TD([[makeQuery(id+"F3.imprint","IMPRINT",EDGE,{"derivedFrom":subQ0}),-1.0]])]});}
            var Q68;
            {var subQ0=sQuery(id+"F3.wireOp",EDGE,"E7.1.19.3");Q68=makeQuery(id+"F3.imprint","IMPRINT",FACE,{"disambiguationData":[TD([[makeQuery(id+"F3.imprint","IMPRINT",EDGE,{"derivedFrom":subQ0}),-1.0]])]});}
            var Q69;
            {var subQ0=sQuery(id+"F3.wireOp",EDGE,"E7.1.18.3");Q69=makeQuery(id+"F3.imprint","IMPRINT",FACE,{"disambiguationData":[TD([[makeQuery(id+"F3.imprint","IMPRINT",EDGE,{"derivedFrom":subQ0}),-1.0]])]});}
            var Q70;
            {var subQ0=sQuery(id+"F3.wireOp",EDGE,"E7.1.17.3");Q70=makeQuery(id+"F3.imprint","IMPRINT",FACE,{"disambiguationData":[TD([[makeQuery(id+"F3.imprint","IMPRINT",EDGE,{"derivedFrom":subQ0}),-1.0]])]});}
            var Q71;
            {var subQ0=sQuery(id+"F3.wireOp",EDGE,"E7.1.16.3");Q71=makeQuery(id+"F3.imprint","IMPRINT",FACE,{"disambiguationData":[TD([[makeQuery(id+"F3.imprint","IMPRINT",EDGE,{"derivedFrom":subQ0}),-1.0]])]});}
            var Q72;
            {var subQ0=sQuery(id+"F3.wireOp",EDGE,"E7.1.15.3");Q72=makeQuery(id+"F3.imprint","IMPRINT",FACE,{"disambiguationData":[TD([[makeQuery(id+"F3.imprint","IMPRINT",EDGE,{"derivedFrom":subQ0}),-1.0]])]});}
            var Q73;
            {var subQ0=sQuery(id+"F3.wireOp",EDGE,"E7.1.14.3");Q73=makeQuery(id+"F3.imprint","IMPRINT",FACE,{"disambiguationData":[TD([[makeQuery(id+"F3.imprint","IMPRINT",EDGE,{"derivedFrom":subQ0}),-1.0]])]});}
            var Q74;
            {var subQ0=sQuery(id+"F3.wireOp",EDGE,"E7.1.13.3");Q74=makeQuery(id+"F3.imprint","IMPRINT",FACE,{"disambiguationData":[TD([[makeQuery(id+"F3.imprint","IMPRINT",EDGE,{"derivedFrom":subQ0}),-1.0]])]});}
            var Q75;
            {var subQ0=sQuery(id+"F3.wireOp",EDGE,"E7.1.12.3");Q75=makeQuery(id+"F3.imprint","IMPRINT",FACE,{"disambiguationData":[TD([[makeQuery(id+"F3.imprint","IMPRINT",EDGE,{"derivedFrom":subQ0}),-1.0]])]});}
            var Q76;
            {var subQ0=sQuery(id+"F3.wireOp",EDGE,"E7.1.11.3");Q76=makeQuery(id+"F3.imprint","IMPRINT",FACE,{"disambiguationData":[TD([[makeQuery(id+"F3.imprint","IMPRINT",EDGE,{"derivedFrom":subQ0}),-1.0]])]});}
            var Q77;
            {var subQ0=sQuery(id+"F3.wireOp",EDGE,"E7.2.11.3");Q77=makeQuery(id+"F3.imprint","IMPRINT",FACE,{"disambiguationData":[TD([[makeQuery(id+"F3.imprint","IMPRINT",EDGE,{"derivedFrom":subQ0}),-1.0]])]});}
            var Q78;
            {var subQ0=sQuery(id+"F3.wireOp",EDGE,"E7.2.12.3");Q78=makeQuery(id+"F3.imprint","IMPRINT",FACE,{"disambiguationData":[TD([[makeQuery(id+"F3.imprint","IMPRINT",EDGE,{"derivedFrom":subQ0}),-1.0]])]});}
            var Q79;
            {var subQ0=sQuery(id+"F3.wireOp",EDGE,"E7.2.13.3");Q79=makeQuery(id+"F3.imprint","IMPRINT",FACE,{"disambiguationData":[TD([[makeQuery(id+"F3.imprint","IMPRINT",EDGE,{"derivedFrom":subQ0}),-1.0]])]});}
            var Q80;
            {var subQ0=sQuery(id+"F3.wireOp",EDGE,"E7.2.14.3");Q80=makeQuery(id+"F3.imprint","IMPRINT",FACE,{"disambiguationData":[TD([[makeQuery(id+"F3.imprint","IMPRINT",EDGE,{"derivedFrom":subQ0}),-1.0]])]});}
            var Q81;
            {var subQ0=sQuery(id+"F3.wireOp",EDGE,"E7.2.15.3");Q81=makeQuery(id+"F3.imprint","IMPRINT",FACE,{"disambiguationData":[TD([[makeQuery(id+"F3.imprint","IMPRINT",EDGE,{"derivedFrom":subQ0}),-1.0]])]});}
            var Q82;
            {var subQ0=sQuery(id+"F3.wireOp",EDGE,"E7.2.16.3");Q82=makeQuery(id+"F3.imprint","IMPRINT",FACE,{"disambiguationData":[TD([[makeQuery(id+"F3.imprint","IMPRINT",EDGE,{"derivedFrom":subQ0}),-1.0]])]});}
            var Q83;
            {var subQ0=sQuery(id+"F3.wireOp",EDGE,"E7.2.17.3");Q83=makeQuery(id+"F3.imprint","IMPRINT",FACE,{"disambiguationData":[TD([[makeQuery(id+"F3.imprint","IMPRINT",EDGE,{"derivedFrom":subQ0}),-1.0]])]});}
            var Q84;
            {var subQ0=sQuery(id+"F3.wireOp",EDGE,"E7.2.18.3");Q84=makeQuery(id+"F3.imprint","IMPRINT",FACE,{"disambiguationData":[TD([[makeQuery(id+"F3.imprint","IMPRINT",EDGE,{"derivedFrom":subQ0}),-1.0]])]});}
            var Q85;
            {var subQ0=sQuery(id+"F3.wireOp",EDGE,"E7.2.19.3");Q85=makeQuery(id+"F3.imprint","IMPRINT",FACE,{"disambiguationData":[TD([[makeQuery(id+"F3.imprint","IMPRINT",EDGE,{"derivedFrom":subQ0}),-1.0]])]});}
            var Q86;
            {var subQ0=sQuery(id+"F3.wireOp",EDGE,"E7.2.20.3");Q86=makeQuery(id+"F3.imprint","IMPRINT",FACE,{"disambiguationData":[TD([[makeQuery(id+"F3.imprint","IMPRINT",EDGE,{"derivedFrom":subQ0}),-1.0]])]});}
            var Q87;
            {var subQ0=sQuery(id+"F3.wireOp",EDGE,"E7.2.21.3");Q87=makeQuery(id+"F3.imprint","IMPRINT",FACE,{"disambiguationData":[TD([[makeQuery(id+"F3.imprint","IMPRINT",EDGE,{"derivedFrom":subQ0}),-1.0]])]});}
            extrude(context, id + "F4", {"entities" : qUnion([Q0, Q1, Q2, Q3, Q4, Q5, Q6, Q7, Q8, Q9, Q10, Q11, Q12, Q13, Q14, Q15, Q16, Q17, Q18, Q19, Q20, Q21, Q22, Q23, Q24, Q25, Q26, Q27, Q28, Q29, Q30, Q31, Q32, Q33, Q34, Q35, Q36, Q37, Q38, Q39, Q40, Q41, Q42, Q43, Q44, Q45, Q46, Q47, Q48, Q49, Q50, Q51, Q52, Q53, Q54, Q55, Q56, Q57, Q58, Q59, Q60, Q61, Q62, Q63, Q64, Q65, Q66, Q67, Q68, Q69, Q70, Q71, Q72, Q73, Q74, Q75, Q76, Q77, Q78, Q79, Q80, Q81, Q82, Q83, Q84, Q85, Q86, Q87]), "operationType" : NewBodyOperationType.REMOVE, "oppositeDirection" : true, "depth" : 25.4 * mm, "offsetDistance" : 25.4 * mm});
        }
        {
            var Q0;
            {var subQ0=sQuery(id+"F0.wireOp",EDGE,"E0.left");Q0=makeQuery(id+"F2.opExtrude","CAP_EDGE",EDGE,{"disambiguationData":[OSD([subQ0]),TDD([makeQuery(id+"F0.imprint","IMPRINT",EDGE,{"disambiguationData":[TD([[makeQuery(id+"F0.imprint","INTERSECT",VERTEX,{"derivedFrom":[sQuery(id+"F0.wireOp",EDGE,"E0.bottom"),subQ0]}),-1.0]])],"derivedFrom":subQ0})])],"isStart":false});}
            var Q1;
            Q1=makeQuery(id+"F2.opExtrude","CAP_EDGE",EDGE,{"disambiguationData":[OSD([sQuery(id+"F0.wireOp",EDGE,"E0.bottom")])],"isStart":false});
            var Q2;
            {var subQ0=sQuery(id+"F0.wireOp",EDGE,"E0.right");Q2=makeQuery(id+"F2.opExtrude","CAP_EDGE",EDGE,{"disambiguationData":[OSD([subQ0]),TDD([makeQuery(id+"F0.imprint","IMPRINT",EDGE,{"disambiguationData":[TD([[makeQuery(id+"F0.imprint","INTERSECT",VERTEX,{"derivedFrom":[sQuery(id+"F0.wireOp",EDGE,"E0.bottom"),subQ0]}),-1.0]])],"derivedFrom":subQ0})])],"isStart":false});}
            var Q3;
            Q3=makeQuery(id+"F2.opExtrude","CAP_EDGE",EDGE,{"disambiguationData":[OSD([sQuery(id+"F0.wireOp",EDGE,"E5.top")])],"isStart":false});
            var Q4;
            Q4=makeQuery(id+"F2.opExtrude","CAP_EDGE",EDGE,{"disambiguationData":[OSD([sQuery(id+"F0.wireOp",EDGE,"E5.left")])],"isStart":false});
            var Q5;
            Q5=makeQuery(id+"F2.opExtrude","CAP_EDGE",EDGE,{"disambiguationData":[OSD([sQuery(id+"F0.wireOp",EDGE,"E4.top")])],"isStart":false});
            var Q6;
            Q6=makeQuery(id+"F2.opExtrude","CAP_EDGE",EDGE,{"disambiguationData":[OSD([sQuery(id+"F0.wireOp",EDGE,"E4.left")])],"isStart":false});
            var Q7;
            Q7=makeQuery(id+"F2.opExtrude","CAP_EDGE",EDGE,{"disambiguationData":[OSD([sQuery(id+"F0.wireOp",EDGE,"E4.bottom")])],"isStart":false});
            var Q8;
            {var subQ0=sQuery(id+"F0.wireOp",EDGE,"E0.left");Q8=makeQuery(id+"F2.opExtrude","CAP_EDGE",EDGE,{"disambiguationData":[OSD([subQ0]),TDD([makeQuery(id+"F0.imprint","IMPRINT",EDGE,{"disambiguationData":[TD([[makeQuery(id+"F0.imprint","INTERSECT",VERTEX,{"derivedFrom":[sQuery(id+"F0.wireOp",EDGE,"E0.top"),subQ0]}),1.0]])],"derivedFrom":subQ0})])],"isStart":false});}
            var Q9;
            Q9=makeQuery(id+"F2.opExtrude","CAP_EDGE",EDGE,{"disambiguationData":[OSD([sQuery(id+"F0.wireOp",EDGE,"E0.top")])],"isStart":false});
            var Q10;
            {var subQ0=sQuery(id+"F0.wireOp",EDGE,"E0.right");Q10=makeQuery(id+"F2.opExtrude","CAP_EDGE",EDGE,{"disambiguationData":[OSD([subQ0]),TDD([makeQuery(id+"F0.imprint","IMPRINT",EDGE,{"disambiguationData":[TD([[makeQuery(id+"F0.imprint","INTERSECT",VERTEX,{"derivedFrom":[sQuery(id+"F0.wireOp",EDGE,"E0.top"),subQ0]}),1.0]])],"derivedFrom":subQ0})])],"isStart":false});}
            var Q11;
            Q11=makeQuery(id+"F2.opExtrude","CAP_EDGE",EDGE,{"disambiguationData":[OSD([sQuery(id+"F0.wireOp",EDGE,"E5.bottom")])],"isStart":false});
            var Q12;
            Q12=makeQuery(id+"F2.opExtrude","SWEPT_EDGE",EDGE,{"disambiguationData":[OSD([sQuery(id+"F0.wireOp",EDGE,"E0.bottom"),sQuery(id+"F0.wireOp",EDGE,"E0.right")])]});
            var Q13;
            Q13=makeQuery(id+"F2.opExtrude","SWEPT_EDGE",EDGE,{"disambiguationData":[OSD([sQuery(id+"F0.wireOp",EDGE,"E0.bottom"),sQuery(id+"F0.wireOp",EDGE,"E0.left")])]});
            var Q14;
            Q14=makeQuery(id+"F2.opExtrude","SWEPT_EDGE",EDGE,{"disambiguationData":[OSD([sQuery(id+"F0.wireOp",EDGE,"E0.top"),sQuery(id+"F0.wireOp",EDGE,"E0.left")])]});
            var Q15;
            Q15=makeQuery(id+"F2.opExtrude","SWEPT_EDGE",EDGE,{"disambiguationData":[OSD([sQuery(id+"F0.wireOp",EDGE,"E0.top"),sQuery(id+"F0.wireOp",EDGE,"E0.right")])]});
            fillet(context, id + "F5", {"entities" : qUnion([Q0, Q1, Q2, Q3, Q4, Q5, Q6, Q7, Q8, Q9, Q10, Q11, Q12, Q13, Q14, Q15]), "radius" : 3.17 * mm, "tangentPropagation" : true, "allowEdgeOverflow" : false});
        }
        {
            var Q0;
            {var subQ0=sQuery(id+"F0.wireOp",EDGE,"E5.right");var subQ1=sQuery(id+"F0.wireOp",EDGE,"E4.right");var subQ2=sQuery(id+"F0.wireOp",EDGE,"E1.right");var subQ3=sQuery(id+"F0.wireOp",EDGE,"E1.left");var subQ4=sQuery(id+"F0.wireOp",EDGE,"E1.top");var subQ5=sQuery(id+"F0.wireOp",EDGE,"E1.bottom");Q0=makeQuery(id+"F2.boolean.opBoolean","MERGE",FACE,{"derivedFrom":[makeQuery(id+"F1.opExtrude","CAP_FACE",FACE,{"disambiguationData":[OSD([subQ5,subQ4,subQ3,subQ2,subQ1,subQ0])],"isStart":true}),makeQuery(id+"F2.opExtrude","CAP_FACE",FACE,{"disambiguationData":[OSD([sQuery(id+"F0.wireOp",EDGE,"E0.bottom"),sQuery(id+"F0.wireOp",EDGE,"E0.top"),sQuery(id+"F0.wireOp",EDGE,"E0.left"),sQuery(id+"F0.wireOp",EDGE,"E0.right"),subQ5,subQ4,subQ3,subQ2,sQuery(id+"F0.wireOp",EDGE,"E4.bottom"),sQuery(id+"F0.wireOp",EDGE,"E4.top"),sQuery(id+"F0.wireOp",EDGE,"E4.left"),subQ1,sQuery(id+"F0.wireOp",EDGE,"E5.bottom"),sQuery(id+"F0.wireOp",EDGE,"E5.top"),sQuery(id+"F0.wireOp",EDGE,"E5.left"),subQ0])],"isStart":true})]});}
            var sketch = newSketch(context, id + "F6", { "sketchPlane" : qUnion([Q0])});
            skLineSegment(sketch, "E8.bottom", {"start": v(-69.85, -25.14) * mm, "end": v(-63.5, -25.14) * mm});
            skLineSegment(sketch, "E8.top", {"start": v(-69.85, 25.66) * mm, "end": v(-63.5, 25.66) * mm});
            skLineSegment(sketch, "E8.left", {"start": v(-69.85, -25.14) * mm, "end": v(-69.85, 25.66) * mm});
            skLineSegment(sketch, "E8.right", {"start": v(-63.5, -25.14) * mm, "end": v(-63.5, 25.66) * mm});
            skLineSegment(sketch, "E9.bottom", {"start": v(69.85, -25.14) * mm, "end": v(63.5, -25.14) * mm});
            skLineSegment(sketch, "E9.top", {"start": v(69.85, 25.66) * mm, "end": v(63.5, 25.66) * mm});
            skLineSegment(sketch, "E9.left", {"start": v(69.85, -25.14) * mm, "end": v(69.85, 25.66) * mm});
            skLineSegment(sketch, "E9.right", {"start": v(63.5, -25.14) * mm, "end": v(63.5, 25.66) * mm});
            skSolve(sketch);
        }
        {
            var Q0;
            Q0=makeQuery(id+"F6.imprint","IMPRINT",FACE,{"disambiguationData":[TD([[makeQuery(id+"F6.imprint","IMPRINT",EDGE,{"derivedFrom":sQuery(id+"F6.wireOp",EDGE,"E8.bottom")}),1.0]])]});
            var Q1;
            Q1=makeQuery(id+"F6.imprint","IMPRINT",FACE,{"disambiguationData":[TD([[makeQuery(id+"F6.imprint","IMPRINT",EDGE,{"derivedFrom":sQuery(id+"F6.wireOp",EDGE,"E9.bottom")}),-1.0]])]});
            extrude(context, id + "F7", {"entities" : qUnion([Q0, Q1]), "operationType" : NewBodyOperationType.REMOVE, "oppositeDirection" : true, "depth" : 9.52 * mm, "offsetDistance" : 25.4 * mm});
        }
        {
            var Q0;
            Q0=makeQuery(id+"F1.opExtrude","CAP_FACE",FACE,{"disambiguationData":[OSD([sQuery(id+"F0.wireOp",EDGE,"E1.bottom"),sQuery(id+"F0.wireOp",EDGE,"E1.top"),sQuery(id+"F0.wireOp",EDGE,"E1.left"),sQuery(id+"F0.wireOp",EDGE,"E1.right"),sQuery(id+"F0.wireOp",EDGE,"E4.right"),sQuery(id+"F0.wireOp",EDGE,"E5.right")])],"isStart":false});
            chamfer(context, id + "F8", {"entities" : qUnion([Q0]), "width" : 1.27 * mm, "tangentPropagation" : true});
        }
        {
            var Q0;
            Q0=makeQuery(id+"F2.opExtrude","SWEPT_FACE",FACE,{"disambiguationData":[OSD([sQuery(id+"F0.wireOp",EDGE,"E0.bottom")])]});
            var sketch = newSketch(context, id + "F9", { "sketchPlane" : qUnion([Q0])});
            skText(sketch, "E10", { "text": "3/16 x 1 w/ Taper\n", "fontName": "OpenSans-Regular.ttf"});
            const initialGuessF9  = {"E10": [-0.05657, 0.0048, 1, 0, 0.00887]};
            skSetInitialGuess(sketch, initialGuessF9);
            skSolve(sketch);
        }
        {
            var Q0;
            Q0 = qSketchRegion(id + "F9", true);
            extrude(context, id + "F10", {"entities" : qUnion([Q0]), "operationType" : NewBodyOperationType.REMOVE, "oppositeDirection" : true, "depth" : 3.17 * mm, "offsetDistance" : 25.4 * mm});
        }
    });
